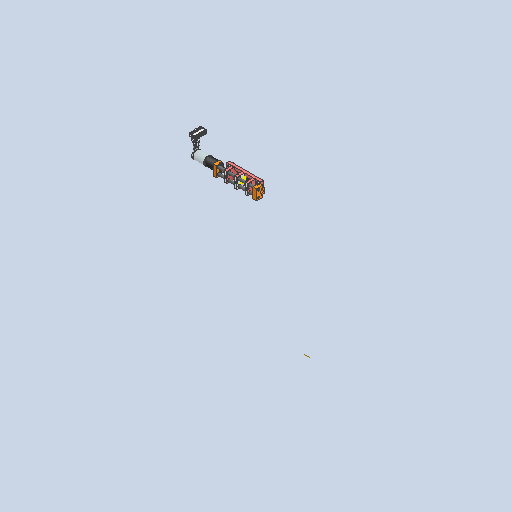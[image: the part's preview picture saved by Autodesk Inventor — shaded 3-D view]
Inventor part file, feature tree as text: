
AUTODESK INVENTOR PART (.ipt)
format: ipt  version: 2023 (Build 270158000, 158)  size: 8,726,528 bytes
history: native  units: mm
features: other x40, sketch x1
ambient origin geometry x8: Origin, YZ Plane, XZ Plane, XY Plane, X Axis, Y Axis, Z Axis, Center Point
bodies: Solid1 (feature_tree)
feature tree (41):
  other  "DifferentialLinearActuator.iam"
  other  "Part1.ipt:1"
  other  "GP16A_2-Stufig-110322.ipt:2"
  other  "283825_ec-max16_5w.ipt:2"
  other  "4145N198_Set Screw Precision Flexible Shaft Couplings.ipt:2"
  other  "91292A832_18-8 Stainless Steel Socket Head Screw.ipt:5"
  other  "91292A832_18-8 Stainless Steel Socket Head Screw.ipt:6"
  other  "MotorMountDifferential.ipt:1"
  other  "91828A113_18-8 Stainless Steel Hex Nut.ipt:1"
  other  "94450A564_Left-Hand Threaded 18-8 Stainless Steel Thin Hex Nut.ipt:3"
  other  "MotorDifferentialMountingBracket.ipt:1"
  other  "POMSliderMotorM25.ipt:1"
  other  "SliderFixtureM25.ipt:1"
  other  "POMSliderMotor.ipt:3"
  other  "POMSliderMotor.ipt:4"
  other  "91292A832_18-8 Stainless Steel Socket Head Screw.ipt:9"
  other  "91292A832_18-8 Stainless Steel Socket Head Screw.ipt:10"
  other  "91292A832_18-8 Stainless Steel Socket Head Screw.ipt:11"
  other  "91292A832_18-8 Stainless Steel Socket Head Screw.ipt:12"
  other  "91292A832_18-8 Stainless Steel Socket Head Screw.ipt:13"
  other  "91292A832_18-8 Stainless Steel Socket Head Screw.ipt:14"
  other  "91292A832_18-8 Stainless Steel Socket Head Screw.ipt:15"
  other  "91292A832_18-8 Stainless Steel Socket Head Screw.ipt:16"
  other  "91292A832_18-8 Stainless Steel Socket Head Screw.ipt:17"
  other  "91292A832_18-8 Stainless Steel Socket Head Screw.ipt:18"
  other  "AxisLinear.ipt:1"
  other  "AxisLinear.ipt:2"
  other  "91292A832_18-8 Stainless Steel Socket Head Screw.ipt:19"
  other  "91292A832_18-8 Stainless Steel Socket Head Screw.ipt:20"
  other  "MotorMountDifferential.ipt:2"
  other  "91292A832_18-8 Stainless Steel Socket Head Screw.ipt:21"
  other  "91292A832_18-8 Stainless Steel Socket Head Screw.ipt:22"
  other  "POMSliderAxis.ipt:1"
  other  "POMSliderAxis.ipt:2"
  other  "POMSliderAxis.ipt:3"
  other  "91292A832_18-8 Stainless Steel Socket Head Screw.ipt:23"
  other  "91292A832_18-8 Stainless Steel Socket Head Screw.ipt:24"
  other  "91292A832_18-8 Stainless Steel Socket Head Screw.ipt:25"
  other  "Screw.ipt:1"
  other  "Work Axis1"
  sketch  "Sketch6"  dims[d0=10.0mm]
